# Revit family: Bodenendblech
name_source: partatom
category: Generic Models
revit_build: Autodesk Revit 2015 (Build: 20140606_1530(x64)
units: mm (PartAtom-declared; Revit-internal decimal feet)

## types (28) — shared parameters
Manufacturer = OBO Bettermann
URL = http://www.obo-bettermann.com

## per-type parameters (varying)
| type | Cut's number | GTIN | Length | Manufacturer Art.No. | Material |
| BEB 100 FS | 2 | 4012196231072 | 93 mm  [stored 0.305118 ft] | 7083106 | Strip-galvanised |
| BEB 150 FS | 4 | 4012196231133 | 143 mm | 7083157 | Strip-galvanised |
| BEB 200 FS | 6 | 4012196231195 | 193 mm  [stored 0.633202 ft] | 7083203 | Strip-galvanised |
| BEB 300 FS | 10 | 4012196231256 | 293 mm | 7083300 | Strip-galvanised |
| BEB 400 FS | 14 | 4012196231317 | 393 mm  [stored 1.28937 ft] | 7083408 | Strip-galvanised |
| BEB 500 FS | 18 | 4012196231379 | 493 mm  [stored 1.61745 ft] | 7083505 | Strip-galvanised |
| BEB 600 FS | 22 | 4012196231492 | 593 mm  [stored 1.94554 ft] | 7083602 | Strip-galvanised |
| BEB 100 DD | 2 | 4012196983728 | 93 mm  [stored 0.305118 ft] | 7083618 | Strip galvanised zinc/aluminium, Double Dip |
| BEB 150 DD | 4 | 4012196026883 | 143 mm | 7083622 | Strip galvanised zinc/aluminium, Double Dip |
| BEB 200 DD | 6 | 4012196982943 | 193 mm  [stored 0.633202 ft] | 7083626 | Strip galvanised zinc/aluminium, Double Dip |
| BEB 300 DD | 10 | 4012196982882 | 293 mm | 7083630 | Strip galvanised zinc/aluminium, Double Dip |
| BEB 400 DD | 14 | 4012196024254 | 393 mm  [stored 1.28937 ft] | 7083634 | Strip galvanised zinc/aluminium, Double Dip |
| BEB 500 DD | 18 | 4012196024490 | 493 mm  [stored 1.61745 ft] | 7083638 | Strip galvanised zinc/aluminium, Double Dip |
| BEB 600 DD | 22 | 4012196034635 | 593 mm  [stored 1.94554 ft] | 7083642 | Strip galvanised zinc/aluminium, Double Dip |
| BEB 100 A2 | 2 | 4012196232031 | 93 mm  [stored 0.305118 ft] | 7084013 | Stainless Steel, A2 |
| BEB 150 A2 | 4 | 4012195995531 | 143 mm | 7084015 | Stainless Steel, A2 |
| BEB 200 A2 | 6 | 4012196232093 | 193 mm  [stored 0.633202 ft] | 7084048 | Stainless Steel, A2 |
| BEB 300 A2 | 10 | 4012196232154 | 293 mm | 7084064 | Stainless Steel, A2 |
| BEB 400 A2 | 14 | 4012196232215 | 393 mm  [stored 1.28937 ft] | 7084080 | Stainless Steel, A2 |
| BEB 500 A2 | 18 | 4012196232277 | 493 mm  [stored 1.61745 ft] | 7084102 | Stainless Steel, A2 |
| BEB 600 A2 | 22 | 4012196232338 | 593 mm  [stored 1.94554 ft] | 7084129 | Stainless Steel, A2 |
| BEB 100 A4 | 2 | 4012195866336 | 93 mm  [stored 0.305118 ft] | 7084141 | Stainless Steel, A4 |
| BEB 150 A4 | 4 | 4012195995548 | 143 mm | 7084142 | Stainless Steel, A4 |
| BEB 200 A4 | 6 | 4012195866343 | 193 mm  [stored 0.633202 ft] | 7084143 | Stainless Steel, A4 |
| BEB 300 A4 | 10 | 4012195866350 | 293 mm | 7084145 | Stainless Steel, A4 |
| BEB 400 A4 | 14 | 4012195866367 | 393 mm  [stored 1.28937 ft] | 7084147 | Stainless Steel, A4 |
| BEB 500 A4 | 18 | 4012195866374 | 493 mm  [stored 1.61745 ft] | 7084149 | Stainless Steel, A4 |
| BEB 600 A4 | 22 | 4012195866381 | 593 mm  [stored 1.94554 ft] | 7084151 | Stainless Steel, A4 |

note: column(s) folded — value = type name in every type: Article Type

note: [stored X ft] marks values corroborated as IEEE doubles in the binary element streams (Revit-internal decimal feet)

## geometry (parser evidence)
native form markers: Sweep x2
no freeform markers — native parametric forms only
